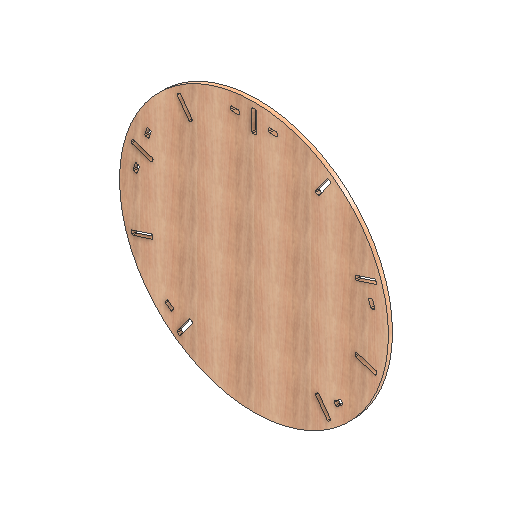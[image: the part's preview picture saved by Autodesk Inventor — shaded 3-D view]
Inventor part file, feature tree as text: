
AUTODESK INVENTOR PART (.ipt)
format: ipt  version: 2021 (Build 250183000, 183)  size: 434,176 bytes
history: native  units: mm
features: other x2, extrude x2, hole x1
ambient origin geometry x8: Origin, YZ Plane, XZ Plane, XY Plane, X Axis, Y Axis, Z Axis, Center Point
bodies: Solid1 (feature_tree)
feature tree (5):
  other  "CONTOURS"
  hole  "HOLES"  [1 undecoded]
  other  "LETTERS"
  extrude  "Extrusion1"  Depth=18.0mm TaperAngle=0.0deg
  extrude  "Extrusion3"  [1 undecoded]
note: 2 required parameter values undecoded (feature->parameter linkage not recoverable at this tier; creation-order binding heuristic only, values carry confidence <= 0.55)
